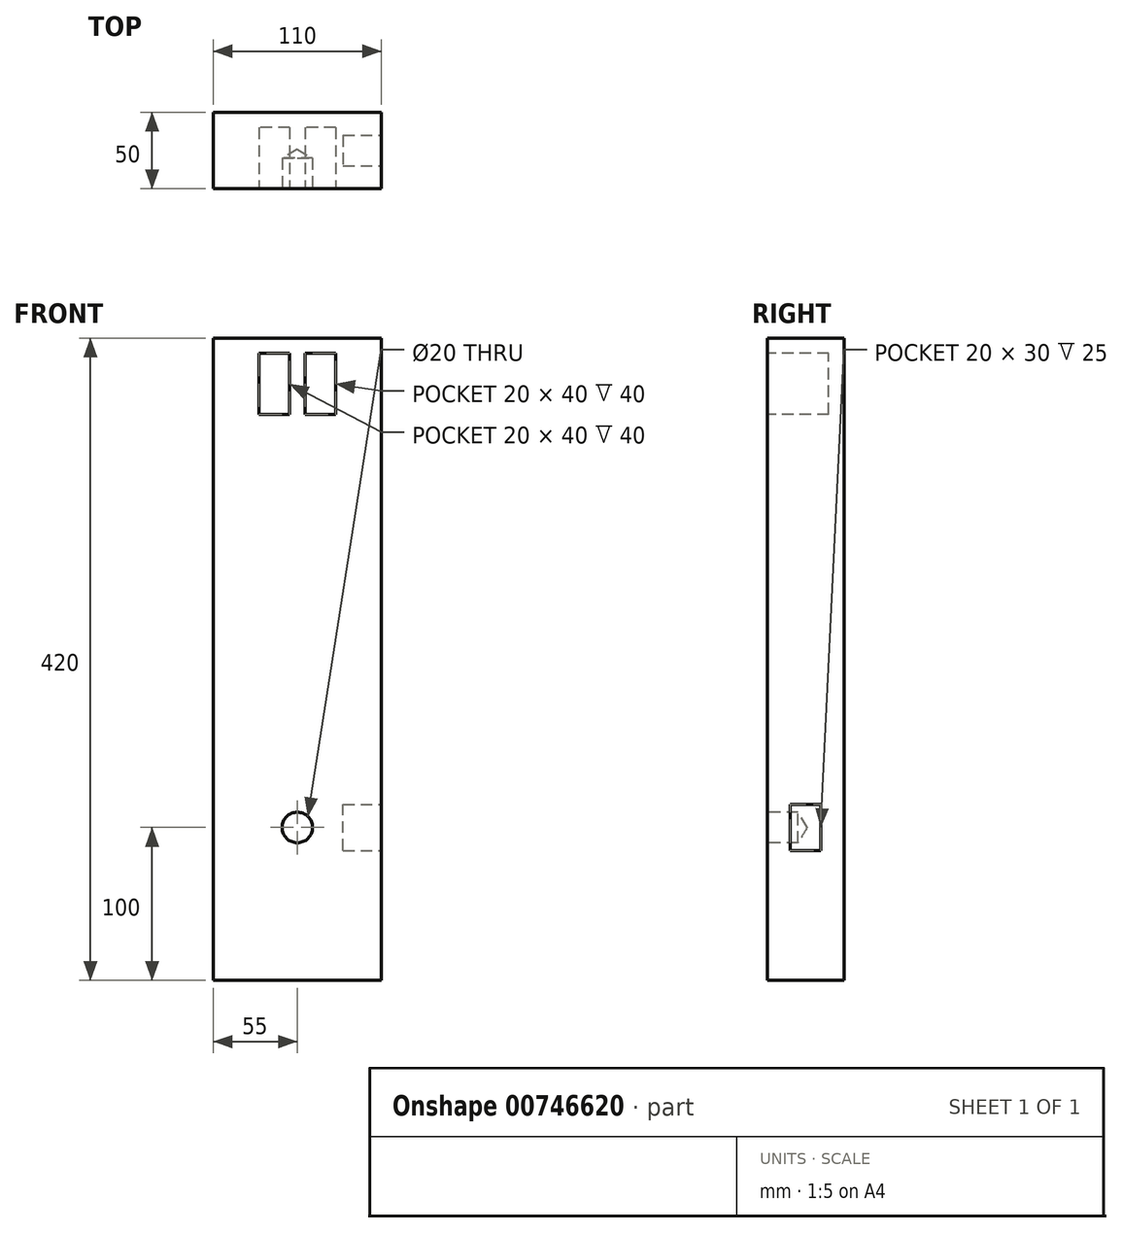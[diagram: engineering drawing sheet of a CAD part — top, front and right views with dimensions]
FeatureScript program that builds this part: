
annotation { "Feature Type Name" : "Feature", "Feature Type Description" : "" }
export const myFeature = defineFeature(function(context is Context, id is Id, definition is map)
    precondition{}
    {
        {
            var Q0;
            Q0=qCreatedBy(makeId("Front.planeOp"),FACE);
            var sketch = newSketch(context, id + "F0", { "sketchPlane" : qUnion([Q0])});
            skLineSegment(sketch, "E0.bottom", {"start": v(55, -210) * mm, "end": v(-55, -210) * mm});
            skLineSegment(sketch, "E0.top", {"start": v(55, 210) * mm, "end": v(-55, 210) * mm});
            skLineSegment(sketch, "E0.left", {"start": v(55, -210) * mm, "end": v(55, 210) * mm});
            skLineSegment(sketch, "E0.right", {"start": v(-55, -210) * mm, "end": v(-55, 210) * mm});
            skPoint(sketch, "E0.middle", {"position": v(0, 0) * mm});
            skSolve(sketch);
        }
        {
            var Q0;
            Q0=qSketchRegion(id+"F0",true);
            extrude(context, id + "F1", {"entities" : qUnion([Q0]), "oppositeDirection" : true, "depth" : 50 * mm, "offsetDistance" : 25 * mm});
        }
        {
            var Q0;
            Q0=makeQuery(id+"F1.opExtrude","CAP_FACE",FACE,{"disambiguationData":[OSD([sQuery(id+"F0.wireOp",EDGE,"E0.bottom"),sQuery(id+"F0.wireOp",EDGE,"E0.top"),sQuery(id+"F0.wireOp",EDGE,"E0.left"),sQuery(id+"F0.wireOp",EDGE,"E0.right")])],"isStart":true});
            var sketch = newSketch(context, id + "F2", { "sketchPlane" : qUnion([Q0])});
            skPoint(sketch, "E1", {"position": v(0, -110) * mm});
            skPoint(sketch, "E2", {"position": v(-15, 180) * mm});
            skPoint(sketch, "E3", {"position": v(15, 180) * mm});
            skLineSegment(sketch, "E4.bottom", {"start": v(-5, 160) * mm, "end": v(-25, 160) * mm});
            skLineSegment(sketch, "E4.top", {"start": v(-5, 200) * mm, "end": v(-25, 200) * mm});
            skLineSegment(sketch, "E4.left", {"start": v(-5, 160) * mm, "end": v(-5, 200) * mm});
            skLineSegment(sketch, "E4.right", {"start": v(-25, 160) * mm, "end": v(-25, 200) * mm});
            skLineSegment(sketch, "E5.bottom", {"start": v(25, 160) * mm, "end": v(5, 160) * mm});
            skLineSegment(sketch, "E5.top", {"start": v(25, 200) * mm, "end": v(5, 200) * mm});
            skLineSegment(sketch, "E5.left", {"start": v(25, 160) * mm, "end": v(25, 200) * mm});
            skLineSegment(sketch, "E5.right", {"start": v(5, 160) * mm, "end": v(5, 200) * mm});
            skSolve(sketch);
        }
        {
            var Q0;
            Q0=sQuery(id+"F2.wireOp",VERTEX,"E1");
            var Q1;
            Q1=makeQuery(id+"F1.opExtrude","SWEPT_BODY",BODY,{"disambiguationData":[OSD([sQuery(id+"F0.wireOp",EDGE,"E0.bottom"),sQuery(id+"F0.wireOp",EDGE,"E0.top"),sQuery(id+"F0.wireOp",EDGE,"E0.left"),sQuery(id+"F0.wireOp",EDGE,"E0.right")])]});
            hole(context, id + "F3", {"style" : HoleStyle.SIMPLE, "endStyle" : HoleEndStyle.BLIND, "holeDiameter" : 20 * mm, "majorDiameter" : 5 * mm, "holeDepth" : 20 * mm, "isTappedThrough" : true, "tappedDepth" : 12 * mm, "tapClearance" : 3, "locations" : qUnion([Q0]), "scope" : qUnion([Q1])});
        }
        {
            var Q0;
            Q0=makeQuery(id+"F2.imprint","IMPRINT",FACE,{"disambiguationData":[TD([[makeQuery(id+"F2.imprint","IMPRINT",EDGE,{"derivedFrom":sQuery(id+"F2.wireOp",EDGE,"E4.bottom")}),-1.0]])]});
            var Q1;
            Q1=makeQuery(id+"F2.imprint","IMPRINT",FACE,{"disambiguationData":[TD([[makeQuery(id+"F2.imprint","IMPRINT",EDGE,{"derivedFrom":sQuery(id+"F2.wireOp",EDGE,"E5.bottom")}),-1.0]])]});
            extrude(context, id + "F4", {"entities" : qUnion([Q0, Q1]), "operationType" : NewBodyOperationType.REMOVE, "oppositeDirection" : true, "depth" : 40 * mm, "offsetDistance" : 25 * mm});
        }
        {
            var Q0;
            Q0=makeQuery(id+"F1.opExtrude","SWEPT_FACE",FACE,{"disambiguationData":[OSD([sQuery(id+"F0.wireOp",EDGE,"E0.left")])]});
            var sketch = newSketch(context, id + "F5", { "sketchPlane" : qUnion([Q0])});
            skLineSegment(sketch, "E6.bottom", {"start": v(35, -125) * mm, "end": v(15, -125) * mm});
            skLineSegment(sketch, "E6.top", {"start": v(35, -95) * mm, "end": v(15, -95) * mm});
            skLineSegment(sketch, "E6.left", {"start": v(35, -125) * mm, "end": v(35, -95) * mm});
            skLineSegment(sketch, "E6.right", {"start": v(15, -125) * mm, "end": v(15, -95) * mm});
            skPoint(sketch, "E6.middle", {"position": v(25, -110) * mm});
            skSolve(sketch);
        }
        {
            var Q0;
            Q0=makeQuery(id+"F5.imprint","IMPRINT",FACE,{"disambiguationData":[TD([[makeQuery(id+"F5.imprint","IMPRINT",EDGE,{"derivedFrom":sQuery(id+"F5.wireOp",EDGE,"E6.bottom")}),-1.0]])]});
            extrude(context, id + "F6", {"entities" : qUnion([Q0]), "operationType" : NewBodyOperationType.REMOVE, "oppositeDirection" : true, "depth" : 25 * mm, "offsetDistance" : 25 * mm});
        }
    });
